# Revit family: Toilet_Tank-In_Wall-KOHLER-Carrier_System-K-6284
name_source: partatom
category: Plumbing Fixtures
revit_build: Autodesk Revit 2015 (Build: 20140606_1530(x64)
units: mm (PartAtom-declared; Revit-internal decimal feet)

## types (1)
- In-Wall Tank and Carrier System
    ADA Compliant = No
    Assembly Code = D2010100
    CW Connection = Yes
    Cold Water Inlet = Cold Water Inlet
    Date Modified = 02/19/2019
    Default Elevation = 0"
    Description = 2 inchx6 inch in-wall tank and carrier system with flush actuator plate
    Finish = Kohler-Metal-NA-Stainless
    Flow Rate = 0 GPM
    Flush Rate = 1.6 GPF
    HW Connection = No
    Hot Water Inlet = Hot Water Inlet
    Length = 5 1/2"
    Manufacturer = KOHLER Co.
    MasterFormat 1995 = 15410
    MasterFormat 2004 = 22.41.13
    Material = Robust Steel Tube Frame
    Model = K-6284-NA
    Pressure = 80.00 psi
    Product Documentation Link = https://www.us.kohler.com
    Product Name = Carrier_System
    Product Page URL = http://www.us.kohler.com
    URL = https://www.us.kohler.com
    Vent Connection = No
    Waste Connection = Yes
    Waste Water Outlet = Waste Water Outlet
    WaterSense Certified = Yes
    Width = 18 13/16"

## geometry (parser evidence)
native form markers: Sweep x6
no freeform markers — native parametric forms only
